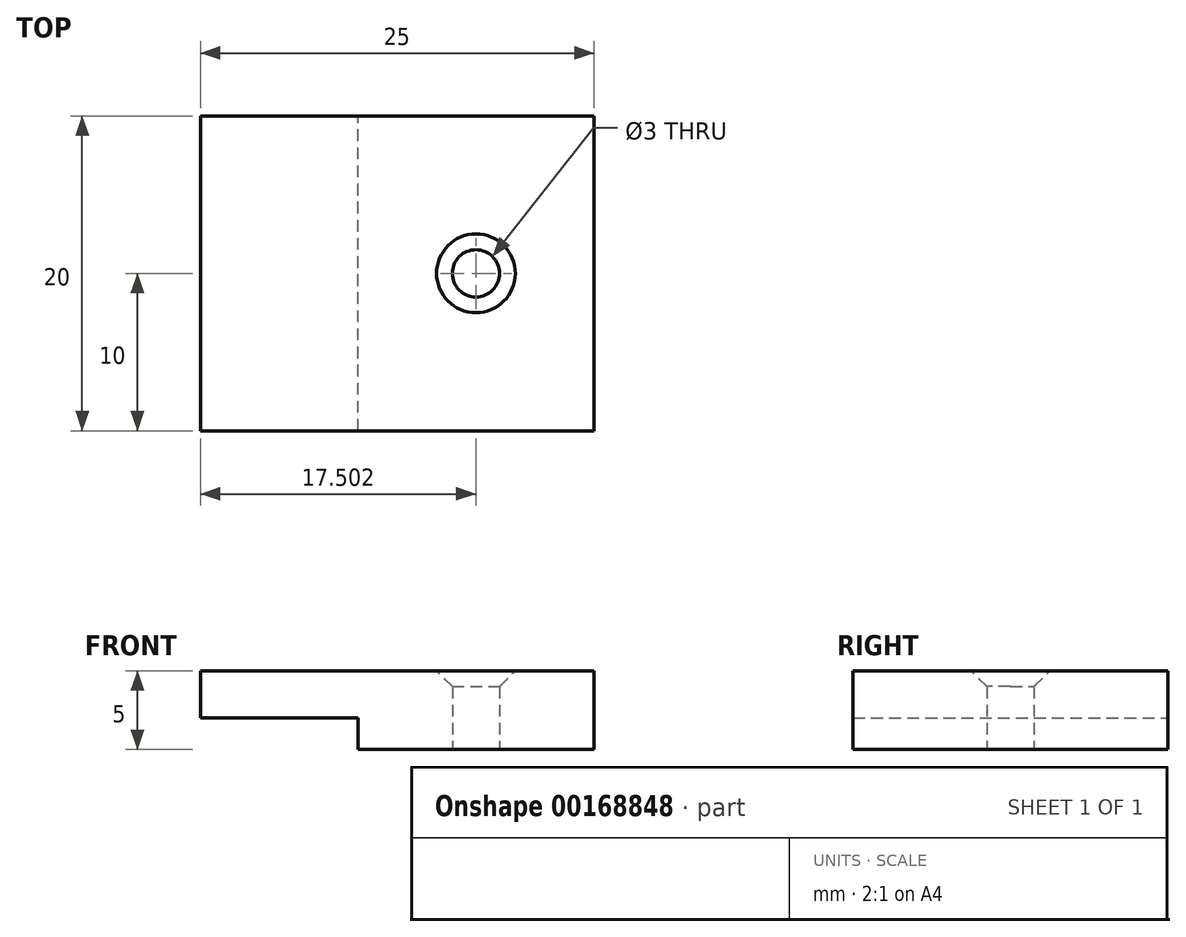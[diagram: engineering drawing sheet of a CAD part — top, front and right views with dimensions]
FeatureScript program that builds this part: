
annotation { "Feature Type Name" : "Feature", "Feature Type Description" : "" }
export const myFeature = defineFeature(function(context is Context, id is Id, definition is map)
    precondition{}
    {
        {
            var Q0;
            Q0=qCreatedBy(makeId("Front.planeOp"),FACE);
            var sketch = newSketch(context, id + "F0", { "sketchPlane" : qUnion([Q0])});
            skLineSegment(sketch, "E0", {"start": v(-12.63, -7.18) * mm, "end": v(-12.63, -9.18) * mm});
            skLineSegment(sketch, "E1", {"start": v(-12.63, -9.18) * mm, "end": v(2.37, -9.18) * mm});
            skLineSegment(sketch, "E2", {"start": v(-12.63, -7.18) * mm, "end": v(-22.63, -7.18) * mm});
            skLineSegment(sketch, "E3", {"start": v(-22.63, -7.18) * mm, "end": v(-22.63, -4.18) * mm});
            skLineSegment(sketch, "E4", {"start": v(-22.63, -4.18) * mm, "end": v(2.37, -4.18) * mm});
            skLineSegment(sketch, "E5", {"start": v(2.37, -4.18) * mm, "end": v(2.37, -9.18) * mm});
            skSolve(sketch);
        }
        {
            var Q0;
            Q0=makeQuery(id+"F0.imprint","IMPRINT",FACE,{"disambiguationData":[TD([[makeQuery(id+"F0.imprint","IMPRINT",EDGE,{"derivedFrom":sQuery(id+"F0.wireOp",EDGE,"E0")}),1.0]])]});
            extrude(context, id + "F1", {"entities" : qUnion([Q0]), "depth" : 20 * mm});
        }
        {
            var Q0;
            Q0=makeQuery(id+"F1.opExtrude","SWEPT_FACE",FACE,{"disambiguationData":[OSD([sQuery(id+"F0.wireOp",EDGE,"E1")])]});
            var sketch = newSketch(context, id + "F2", { "sketchPlane" : qUnion([Q0])});
            skLineSegment(sketch, "E6.bottom", {"start": v(-12.63, 20) * mm, "end": v(-12.63, 20) * mm});
            skLineSegment(sketch, "E6.top", {"start": v(-12.63, 0) * mm, "end": v(-12.63, 0) * mm});
            skLineSegment(sketch, "E6.left", {"start": v(-12.63, 20) * mm, "end": v(-12.63, 0) * mm});
            skLineSegment(sketch, "E6.right", {"start": v(-12.63, 20) * mm, "end": v(-12.63, 0) * mm});
            skLineSegment(sketch, "E7.bottom", {"start": v(2.37, 0) * mm, "end": v(-12.63, 0) * mm, "construction": true});
            skLineSegment(sketch, "E7.top", {"start": v(2.37, 20) * mm, "end": v(-12.63, 20) * mm, "construction": true});
            skLineSegment(sketch, "E7.left", {"start": v(2.37, 0) * mm, "end": v(2.37, 20) * mm, "construction": true});
            skLineSegment(sketch, "E7.right", {"start": v(-12.63, 0) * mm, "end": v(-12.63, 20) * mm, "construction": true});
            skPoint(sketch, "E8.centerSnap0", {"position": v(-5.13, 0) * mm});
            skPoint(sketch, "E8.centerSnap1", {"position": v(2.37, 10) * mm});
            skCircle(sketch, "E9", {"center": v(-5.13, 10) * mm, "radius": 1.5 * mm});
            skSolve(sketch);
        }
        {
            var Q0;
            Q0=makeQuery(id+"F2.imprint","IMPRINT",FACE,{"disambiguationData":[TD([[makeQuery(id+"F2.imprint","IMPRINT",EDGE,{"derivedFrom":sQuery(id+"F2.wireOp",EDGE,"E9")}),1.0]])]});
            extrude(context, id + "F3", {"entities" : qUnion([Q0]), "operationType" : NewBodyOperationType.REMOVE, "endBound" : BoundingType.THROUGH_ALL, "oppositeDirection" : true, "depth" : 4 * mm});
        }
        {
            var Q0;
            Q0=makeQuery(id+"F3.boolean.opBoolean","INTERSECT",EDGE,{"derivedFrom":[makeQuery(id+"F1.opExtrude","SWEPT_FACE",FACE,{"disambiguationData":[OSD([sQuery(id+"F0.wireOp",EDGE,"E4")])]}),makeQuery(id+"F3.opExtrude","SWEPT_FACE",FACE,{"disambiguationData":[OSD([sQuery(id+"F2.wireOp",EDGE,"E9")])]})]});
            chamfer(context, id + "F4", {"entities" : qUnion([Q0]), "width" : 1 * mm, "tangentPropagation" : true});
        }
    });
